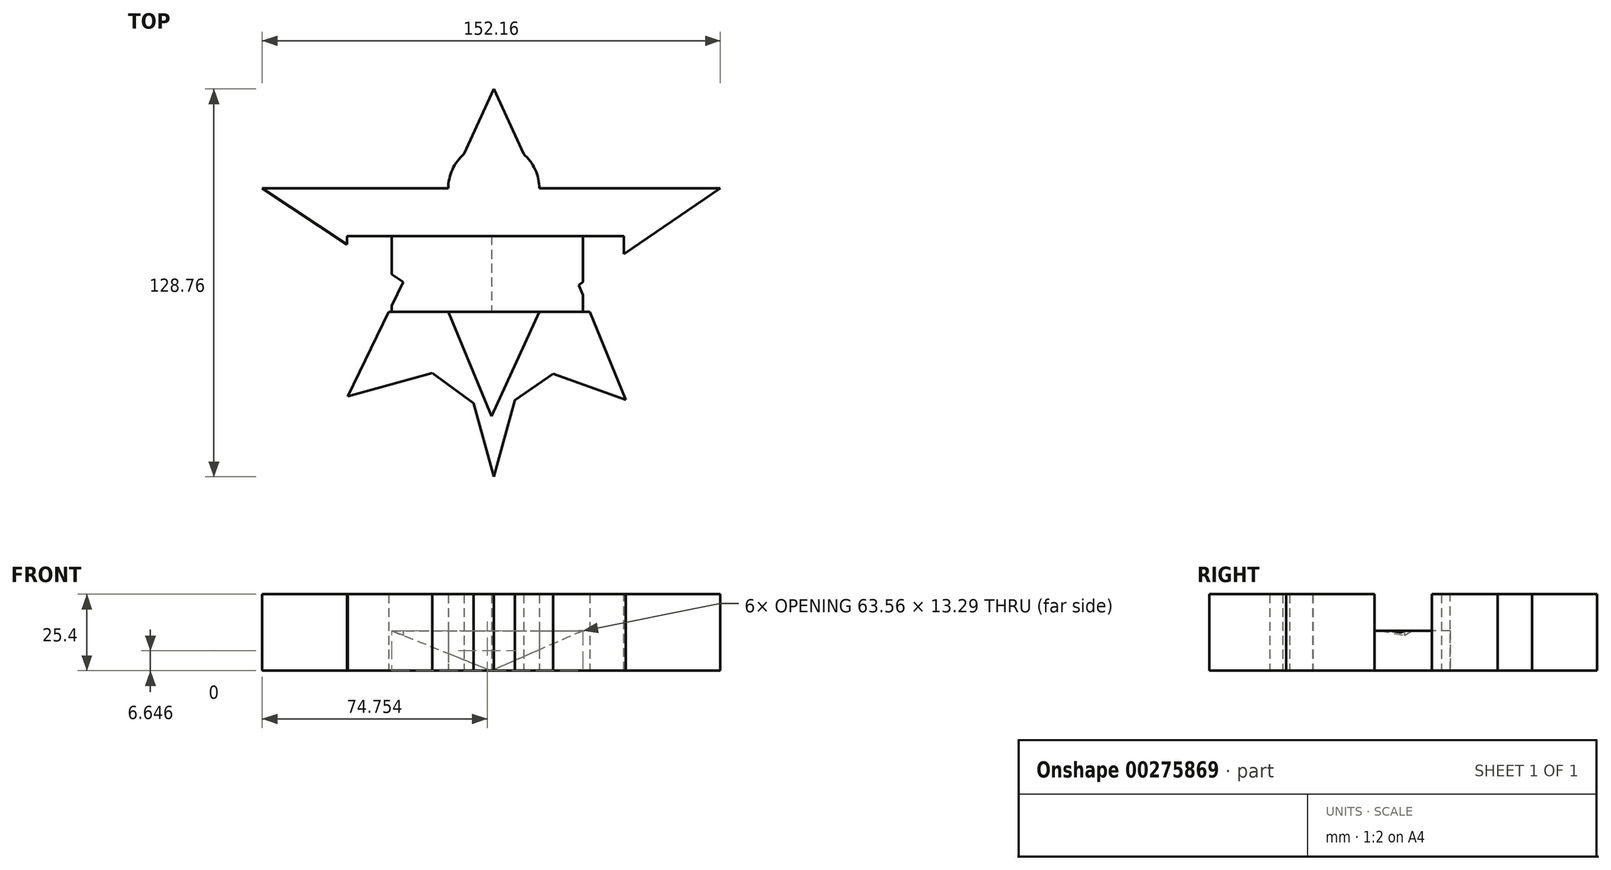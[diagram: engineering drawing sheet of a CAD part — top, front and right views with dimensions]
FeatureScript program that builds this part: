
annotation { "Feature Type Name" : "Feature", "Feature Type Description" : "" }
export const myFeature = defineFeature(function(context is Context, id is Id, definition is map)
    precondition{}
    {
        {
            var Q0;
            Q0=qCreatedBy(makeId("Top.planeOp"),FACE);
            var sketch = newSketch(context, id + "F0", { "sketchPlane" : qUnion([Q0])});
            skLineSegment(sketch, "E0.bottom", {"start": v(0, 0) * mm, "end": v(-14.35, 0) * mm});
            skLineSegment(sketch, "E0.top", {"start": v(0, 40.92) * mm, "end": v(-14.35, 40.92) * mm});
            skLineSegment(sketch, "E0.left", {"start": v(0, 0) * mm, "end": v(0, 40.92) * mm});
            skLineSegment(sketch, "E0.right", {"start": v(-14.35, 0) * mm, "end": v(-14.35, 40.92) * mm});
            skLineSegment(sketch, "E1.bottom", {"start": v(0, 0) * mm, "end": v(15.9, 0) * mm});
            skLineSegment(sketch, "E1.top", {"start": v(0, 40.92) * mm, "end": v(15.9, 40.92) * mm});
            skLineSegment(sketch, "E1.right", {"start": v(15.9, 0) * mm, "end": v(15.9, 40.92) * mm});
            skLineSegment(sketch, "E2", {"start": v(-14.35, 40.92) * mm, "end": v(-47.71, -28.12) * mm});
            skLineSegment(sketch, "E3", {"start": v(-47.71, -28.12) * mm, "end": v(-14.35, 0) * mm});
            skLineSegment(sketch, "E4", {"start": v(15.9, 40.92) * mm, "end": v(44.61, -29.29) * mm});
            skLineSegment(sketch, "E5", {"start": v(44.61, -29.29) * mm, "end": v(15.9, 0) * mm});
            skLineSegment(sketch, "E6", {"start": v(15.9, 0) * mm, "end": v(0, -34.72) * mm});
            skLineSegment(sketch, "E7", {"start": v(-14.35, 0) * mm, "end": v(0, -34.72) * mm});
            skArc(sketch, "E8", {"start": v(15.9, 40.92) * mm, "mid": v(0.78, 56.05) * mm, "end": v(-14.35, 40.92) * mm});
            skLineSegment(sketch, "E9", {"start": v(-19.68, -20.39) * mm, "end": v(0, -34.72) * mm});
            skLineSegment(sketch, "E10", {"start": v(0, -34.72) * mm, "end": v(20.52, -20.56) * mm});
            skLineSegment(sketch, "E11", {"start": v(20.52, -20.56) * mm, "end": v(44.61, -29.29) * mm});
            skLineSegment(sketch, "E12", {"start": v(-19.68, -20.39) * mm, "end": v(-47.71, -28.12) * mm});
            skLineSegment(sketch, "E13", {"start": v(15.9, 40.92) * mm, "end": v(76, 40.92) * mm});
            skLineSegment(sketch, "E14", {"start": v(-14.35, 40.92) * mm, "end": v(-76.15, 40.92) * mm});
            skLineSegment(sketch, "E15", {"start": v(-76.15, 40.92) * mm, "end": v(-14.35, 0) * mm});
            skLineSegment(sketch, "E16", {"start": v(76, 40.92) * mm, "end": v(15.9, 0) * mm});
            skLineSegment(sketch, "E17", {"start": v(-14.35, 0) * mm, "end": v(0.78, -54.81) * mm});
            skLineSegment(sketch, "E18", {"start": v(0.78, -54.81) * mm, "end": v(15.9, 0) * mm});
            skLineSegment(sketch, "E19", {"start": v(-14.35, 40.92) * mm, "end": v(0.78, 73.95) * mm});
            skLineSegment(sketch, "E20", {"start": v(0.78, 73.95) * mm, "end": v(15.9, 40.92) * mm});
            skSolve(sketch);
        }
        {
            var Q0;
            Q0 = qSketchRegion(id + "F0", true);
            extrude(context, id + "F1", {"entities" : qUnion([Q0]), "depth" : 25.4 * mm});
        }
        {
            var Q0;
            Q0=qCreatedBy(makeId("Top.planeOp"),FACE);
            var sketch = newSketch(context, id + "F2", { "sketchPlane" : qUnion([Q0])});
            skLineSegment(sketch, "E21", {"start": v(0, 0) * mm, "end": v(-44.7, 28.65) * mm});
            skLineSegment(sketch, "E22", {"start": v(0, 0) * mm, "end": v(43.33, 28.55) * mm});
            skLineSegment(sketch, "E23", {"start": v(43.33, 28.55) * mm, "end": v(-44.7, 28.65) * mm});
            skLineSegment(sketch, "E24", {"start": v(0, 0) * mm, "end": v(0, 17.7) * mm});
            skLineSegment(sketch, "E25", {"start": v(0, 17.7) * mm, "end": v(26.8, 17.66) * mm});
            skLineSegment(sketch, "E26", {"start": v(26.8, 17.66) * mm, "end": v(0, 17.7) * mm});
            skLineSegment(sketch, "E27", {"start": v(0, 17.7) * mm, "end": v(-27.65, 17.72) * mm});
            skLineSegment(sketch, "E28", {"start": v(0, 17.7) * mm, "end": v(43.33, 28.55) * mm});
            skLineSegment(sketch, "E29", {"start": v(0, 17.7) * mm, "end": v(-44.7, 28.65) * mm});
            skSolve(sketch);
        }
        {
            var Q0;
            Q0 = qSketchRegion(id + "F2", true);
            extrude(context, id + "F3", {"entities" : qUnion([Q0]), "operationType" : NewBodyOperationType.REMOVE, "oppositeDirection" : true, "depth" : 36.32 * mm});
        }
        {
            var Q0;
            Q0=qCreatedBy(makeId("Front.planeOp"),FACE);
            var sketch = newSketch(context, id + "F4", { "sketchPlane" : qUnion([Q0])});
            skLineSegment(sketch, "E30", {"start": v(0, 0) * mm, "end": v(-48, 0) * mm});
            skLineSegment(sketch, "E31", {"start": v(-48, 0) * mm, "end": v(0, 0) * mm});
            skLineSegment(sketch, "E32", {"start": v(0, 0) * mm, "end": v(43.96, 0) * mm});
            skLineSegment(sketch, "E33", {"start": v(43.96, 0) * mm, "end": v(-48, 0) * mm});
            skLineSegment(sketch, "E34", {"start": v(-48, 0) * mm, "end": v(-48, 19.23) * mm});
            skLineSegment(sketch, "E35", {"start": v(-48, 19.23) * mm, "end": v(0, 0) * mm});
            skLineSegment(sketch, "E36", {"start": v(43.96, 0) * mm, "end": v(43.96, 19.23) * mm});
            skLineSegment(sketch, "E37", {"start": v(43.96, 19.23) * mm, "end": v(0, 0) * mm});
            skLineSegment(sketch, "E38", {"start": v(-33.18, 13.3) * mm, "end": v(30.38, 13.3) * mm});
            skArc(sketch, "E39", {"start": v(-48, 0) * mm, "mid": v(-2.02, -23.41) * mm, "end": v(43.96, 0) * mm});
            skLineSegment(sketch, "E40", {"start": v(-48, 19.23) * mm, "end": v(0, 36.9) * mm});
            skLineSegment(sketch, "E41", {"start": v(0, 36.9) * mm, "end": v(43.96, 19.23) * mm});
            skLineSegment(sketch, "E42", {"start": v(0, 36.9) * mm, "end": v(0, 13.3) * mm});
            skPoint(sketch, "E42.endSnap0", {"position": v(-1.4, 13.3) * mm});
            skLineSegment(sketch, "E43", {"start": v(-48, 19.23) * mm, "end": v(-48, 56.4) * mm});
            skLineSegment(sketch, "E44", {"start": v(-48, 56.4) * mm, "end": v(0, 56.4) * mm});
            skLineSegment(sketch, "E45", {"start": v(43.96, 19.23) * mm, "end": v(43.96, 56.56) * mm});
            skLineSegment(sketch, "E46", {"start": v(43.96, 56.56) * mm, "end": v(0, 56.4) * mm});
            skSolve(sketch);
        }
        {
            var Q0;
            Q0 = qSketchRegion(id + "F4", true);
            extrude(context, id + "F5", {"entities" : qUnion([Q0]), "operationType" : NewBodyOperationType.REMOVE, "oppositeDirection" : true, "depth" : 25.15 * mm});
        }
    });
